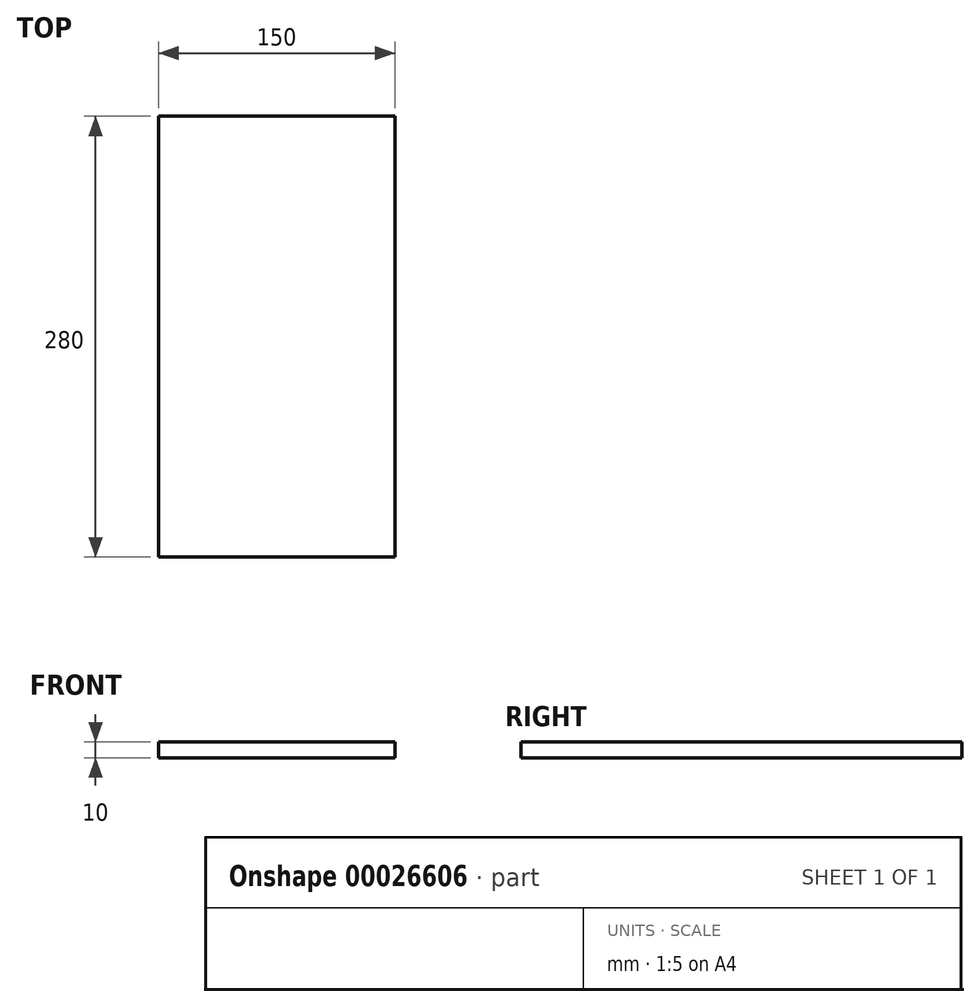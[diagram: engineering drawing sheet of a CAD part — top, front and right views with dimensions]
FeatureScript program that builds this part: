
annotation { "Feature Type Name" : "Feature", "Feature Type Description" : "" }
export const myFeature = defineFeature(function(context is Context, id is Id, definition is map)
    precondition{}
    {
        {
            var Q0;
            Q0=qCreatedBy(makeId("Top.planeOp"),FACE);
            var sketch = newSketch(context, id + "F0", { "sketchPlane" : qUnion([Q0])});
            skLineSegment(sketch, "E0.bottom", {"start": v(-44.88, 138.19) * mm, "end": v(105.12, 138.19) * mm});
            skLineSegment(sketch, "E0.top", {"start": v(-44.88, -141.81) * mm, "end": v(105.12, -141.81) * mm});
            skLineSegment(sketch, "E0.left", {"start": v(-44.88, 138.19) * mm, "end": v(-44.88, -141.81) * mm});
            skLineSegment(sketch, "E0.right", {"start": v(105.12, 138.19) * mm, "end": v(105.12, -141.81) * mm});
            skSolve(sketch);
        }
        {
            var Q0;
            Q0=qSketchRegion(id+"F0",true);
            extrude(context, id + "F1", {"entities" : qUnion([Q0]), "depth" : 10 * mm});
        }
    });
